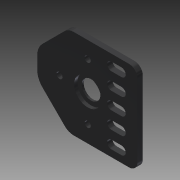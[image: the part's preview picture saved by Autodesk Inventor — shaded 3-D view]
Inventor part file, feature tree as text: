
AUTODESK INVENTOR PART (.ipt)
format: ipt  version: 2014 SP1 (Build 180222100, 222)  size: 194,560 bytes
history: native  units: in
note: dims shown in document units (in); Inventor stores cm internally (conversion verified against a paired STEP export)
features: extrude x5, sketch x5, fillet x3
ambient origin geometry x8: Origin, YZ Plane, XZ Plane, XY Plane, X Axis, Y Axis, Z Axis, Center Point
bodies: Solid1 (feature_tree)
feature tree (13):
  extrude  "Extrusion1"  Depth=2.3343in
  extrude  "Extrusion2"  Depth=2.0866in
  extrude  "Extrusion3"  Depth=1.1811in TaperAngle=180.0deg
  extrude  "Extrusion4"  Depth=0.1248in
  extrude  "Extrusion5"  Depth=0.1969in
  fillet  "Fillet1"  Radius=1.7268in
  fillet  "Fillet2"  Radius=1.1811in
  fillet  "Fillet3"  Radius=0.0787in
  sketch  "Sketch1"  dims[d0=1.1756in d1=2.3343in]
  sketch  "Sketch2"  dims[d2=2.0866in d3=0.4331in]
  sketch  "Sketch3"  dims[d4=0.1248in d5=0.0in d6=1.1811in d8=180.0deg]
  sketch  "Sketch4"  dims[d10=0.1248in d11=0.0in d12=0.6319in]
  sketch  "Sketch5"  dims[d13=0.0787in d14=0.0in d15=0.1969in d16=1.7268in d17=1.1811in d19=0.3937in d20=1.1811in d22=0.3937in d25=0.0787in d26=0.0in d27=45.0deg d28=0.0787in d29=0.0in d30=0.2854in d31=0.4205in d32=0.1969in]
